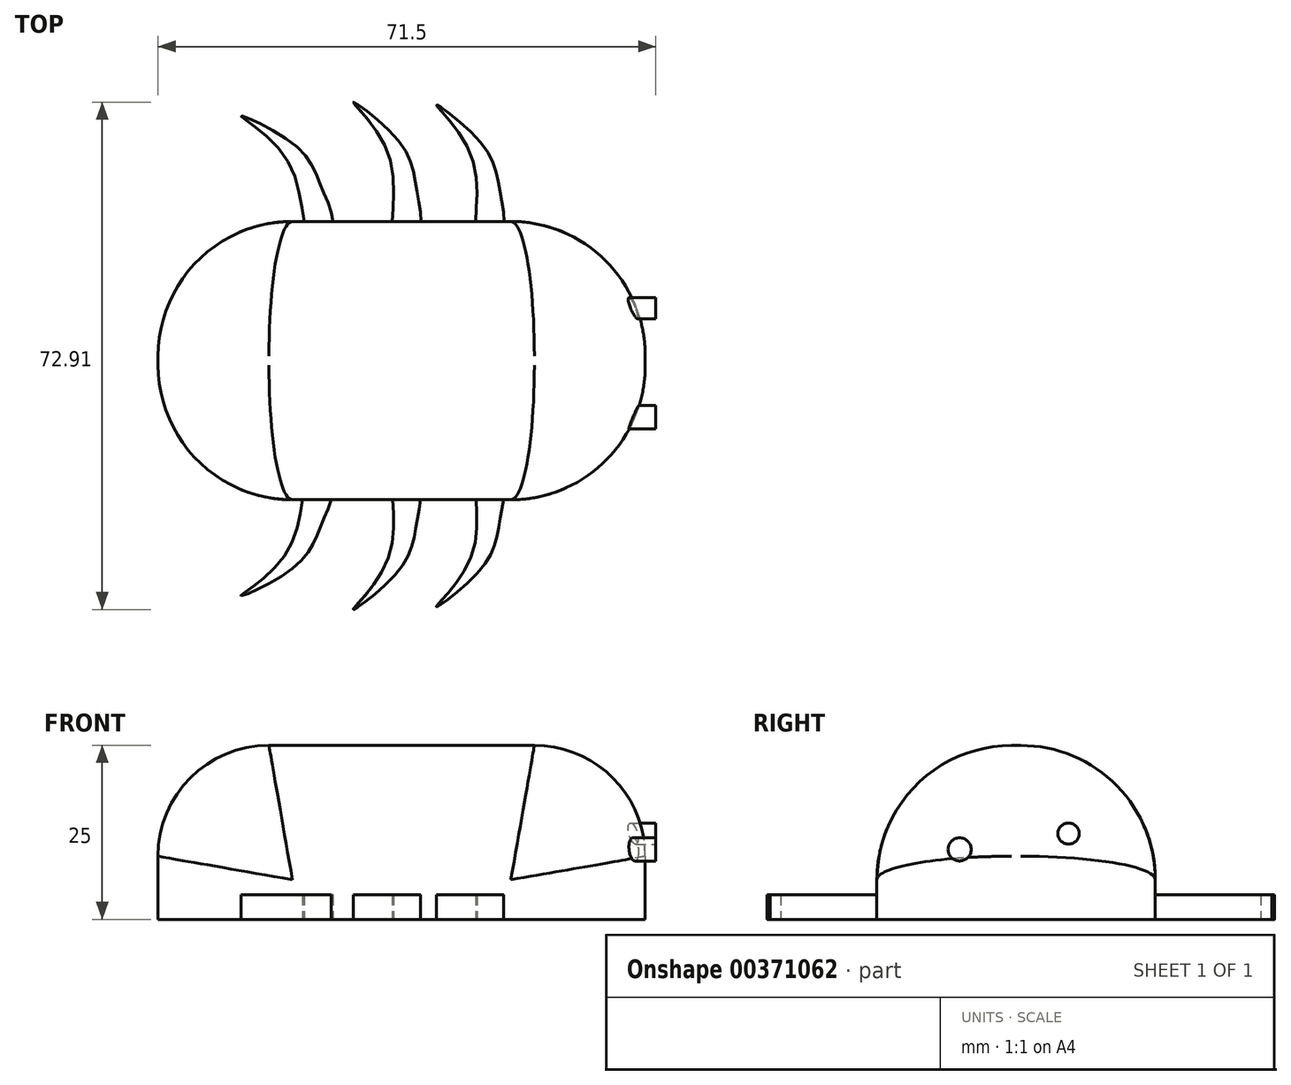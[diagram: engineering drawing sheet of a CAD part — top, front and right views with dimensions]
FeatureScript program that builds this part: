
annotation { "Feature Type Name" : "Feature", "Feature Type Description" : "" }
export const myFeature = defineFeature(function(context is Context, id is Id, definition is map)
    precondition{}
    {
        {
            var Q0;
            Q0=qCreatedBy(makeId("Top.planeOp"),FACE);
            var sketch = newSketch(context, id + "F0", { "sketchPlane" : qUnion([Q0])});
            skLineSegment(sketch, "E0.bottom", {"start": v(-42.42, 27.03) * mm, "end": v(27.58, 27.03) * mm});
            skLineSegment(sketch, "E0.top", {"start": v(-42.42, -12.97) * mm, "end": v(27.58, -12.97) * mm});
            skLineSegment(sketch, "E0.left", {"start": v(-42.42, 27.03) * mm, "end": v(-42.42, -12.97) * mm});
            skLineSegment(sketch, "E0.right", {"start": v(27.58, 27.03) * mm, "end": v(27.58, -12.97) * mm});
            skSolve(sketch);
        }
        {
            var Q0;
            Q0=makeQuery(id+"F0.imprint","IMPRINT",FACE,{"disambiguationData":[TD([[makeQuery(id+"F0.imprint","IMPRINT",EDGE,{"derivedFrom":sQuery(id+"F0.wireOp",EDGE,"E0.bottom")}),-1.0]])]});
            extrude(context, id + "F1", {"entities" : qUnion([Q0]), "depth" : 25 * mm});
        }
        {
            var Q0;
            Q0=makeQuery(id+"F1.opExtrude","CAP_EDGE",EDGE,{"disambiguationData":[OSD([sQuery(id+"F0.wireOp",EDGE,"E0.left")])],"isStart":false});
            var Q1;
            Q1=makeQuery(id+"F1.opExtrude","CAP_EDGE",EDGE,{"disambiguationData":[OSD([sQuery(id+"F0.wireOp",EDGE,"E0.right")])],"isStart":false});
            fillet(context, id + "F2", {"entities" : qUnion([Q0, Q1]), "radius" : 15.93 * mm, "tangentPropagation" : true, "allowEdgeOverflow" : false});
        }
        {
            var Q0;
            {var subQ0=sQuery(id+"F0.wireOp",EDGE,"E0.right");Q0=makeQuery(id+"F2.opFillet","BLEND_EDGE",EDGE,{"blendedFrom":[makeQuery(id+"F1.opExtrude","CAP_EDGE",EDGE,{"disambiguationData":[OSD([subQ0])],"isStart":false}),makeQuery(id+"F1.opExtrude","CAP_FACE",FACE,{"disambiguationData":[OSD([sQuery(id+"F0.wireOp",EDGE,"E0.bottom"),sQuery(id+"F0.wireOp",EDGE,"E0.top"),sQuery(id+"F0.wireOp",EDGE,"E0.left"),subQ0])],"isStart":false})],"blendedInto":[makeQuery(id+"F1.opExtrude","CAP_FACE",FACE,{"disambiguationData":[OSD([sQuery(id+"F0.wireOp",EDGE,"E0.bottom"),sQuery(id+"F0.wireOp",EDGE,"E0.top"),sQuery(id+"F0.wireOp",EDGE,"E0.left"),subQ0])],"isStart":false})]});}
            var Q1;
            Q1=makeQuery(id+"F2.opFillet","BLEND_FACE",FACE,{"disambiguationData":[OSD([sQuery(id+"F0.wireOp",EDGE,"E0.right")])]});
            fillet(context, id + "F3", {"entities" : qUnion([Q0, Q1]), "radius" : 19.3 * mm, "tangentPropagation" : true, "allowEdgeOverflow" : false});
        }
        {
            var Q0;
            Q0=qCreatedBy(makeId("Top.planeOp"),FACE);
            var sketch = newSketch(context, id + "F4", { "sketchPlane" : qUnion([Q0])});
            skFitSpline(sketch, "E1", {"points": [v(6.78, 25) * mm, v(6.78, 30.78) * mm, v(4.26, 38) * mm, v(-2.42, 43.77) * mm, v(2.81, 35.83) * mm, v(3.72, 24.28) * mm, v(6.78, 25) * mm]});
            skFitSpline(sketch, "E2", {"points": [v(-5.18, 25.4) * mm, v(-5.18, 31.18) * mm, v(-7.7, 38.4) * mm, v(-14.38, 44.17) * mm, v(-9.15, 36.23) * mm, v(-8.25, 24.68) * mm, v(-5.18, 25.4) * mm]});
            skFitSpline(sketch, "E3", {"points": [v(-17.51, 25.82) * mm, v(-18.74, 31.46) * mm, v(-22.75, 37.97) * mm, v(-30.5, 42.19) * mm, v(-23.7, 35.55) * mm, v(-20.36, 24.46) * mm, v(-17.51, 25.82) * mm]});
            skFitSpline(sketch, "E4.MirrorC", {"points": [v(6.78, -9.57) * mm, v(6.78, -15.34) * mm, v(4.26, -22.56) * mm, v(-2.42, -28.33) * mm, v(2.81, -20.4) * mm, v(3.72, -8.85) * mm, v(6.78, -9.57) * mm]});
            skFitSpline(sketch, "E5.MirrorC", {"points": [v(-5.18, -9.97) * mm, v(-5.18, -15.75) * mm, v(-7.7, -22.96) * mm, v(-14.38, -28.74) * mm, v(-9.15, -20.8) * mm, v(-8.25, -9.25) * mm, v(-5.18, -9.97) * mm]});
            skFitSpline(sketch, "E6.MirrorC", {"points": [v(-17.51, -10.38) * mm, v(-18.74, -16.02) * mm, v(-22.75, -22.54) * mm, v(-30.5, -26.76) * mm, v(-23.7, -20.11) * mm, v(-20.36, -9.02) * mm, v(-17.51, -10.38) * mm]});
            skSolve(sketch);
        }
        {
            var Q0;
            Q0=makeQuery(id+"F4.imprint","IMPRINT",FACE,{"disambiguationData":[TD([[makeQuery(id+"F4.imprint","IMPRINT",EDGE,{"derivedFrom":sQuery(id+"F4.wireOp",EDGE,"E1")}),1.0]])]});
            var Q1;
            Q1=makeQuery(id+"F4.imprint","IMPRINT",FACE,{"disambiguationData":[TD([[makeQuery(id+"F4.imprint","IMPRINT",EDGE,{"derivedFrom":sQuery(id+"F4.wireOp",EDGE,"E2")}),1.0]])]});
            var Q2;
            Q2=makeQuery(id+"F4.imprint","IMPRINT",FACE,{"disambiguationData":[TD([[makeQuery(id+"F4.imprint","IMPRINT",EDGE,{"derivedFrom":sQuery(id+"F4.wireOp",EDGE,"E3")}),1.0]])]});
            var Q3;
            Q3=makeQuery(id+"F4.imprint","IMPRINT",FACE,{"disambiguationData":[TD([[makeQuery(id+"F4.imprint","IMPRINT",EDGE,{"derivedFrom":sQuery(id+"F4.wireOp",EDGE,"E4.MirrorC")}),-1.0]])]});
            var Q4;
            Q4=makeQuery(id+"F4.imprint","IMPRINT",FACE,{"disambiguationData":[TD([[makeQuery(id+"F4.imprint","IMPRINT",EDGE,{"derivedFrom":sQuery(id+"F4.wireOp",EDGE,"E6.MirrorC")}),-1.0]])]});
            var Q5;
            Q5=makeQuery(id+"F4.imprint","IMPRINT",FACE,{"disambiguationData":[TD([[makeQuery(id+"F4.imprint","IMPRINT",EDGE,{"derivedFrom":sQuery(id+"F4.wireOp",EDGE,"E5.MirrorC")}),-1.0]])]});
            extrude(context, id + "F5", {"entities" : qUnion([Q0, Q1, Q2, Q3, Q4, Q5]), "operationType" : NewBodyOperationType.ADD, "depth" : 3.5 * mm});
        }
        {
            var Q0;
            Q0=makeQuery(id+"F1.opExtrude","SWEPT_FACE",FACE,{"disambiguationData":[OSD([sQuery(id+"F0.wireOp",EDGE,"E0.right")])]});
            var sketch = newSketch(context, id + "F6", { "sketchPlane" : qUnion([Q0])});
            skCircle(sketch, "E7", {"center": v(-1.09, 10.05) * mm, "radius": 1.66 * mm});
            skCircle(sketch, "E8", {"center": v(14.56, 12.32) * mm, "radius": 1.52 * mm});
            skSolve(sketch);
        }
        {
            var Q0;
            Q0 = qSketchRegion(id + "F6", true);
            extrude(context, id + "F7", {"entities" : qUnion([Q0]), "operationType" : NewBodyOperationType.ADD, "oppositeDirection" : true, "depth" : 25 * mm, "hasSecondDirection" : true, "secondDirectionOppositeDirection" : false, "secondDirectionDepth" : 1.5 * mm});
        }
        {
            var Q0;
            Q0=makeQuery(id+"F1.opExtrude","CAP_EDGE",EDGE,{"disambiguationData":[OSD([sQuery(id+"F0.wireOp",EDGE,"E0.right")])],"isStart":true});
            cPlane(context, id + "F8", {"entities" : qUnion([Q0]), "cplaneType" : CPlaneType.LINE_ANGLE, "offset" : 25 * mm, "angle" : 115 * degree, "width" : 150 * mm, "height" : 150 * mm});
        }
    });
